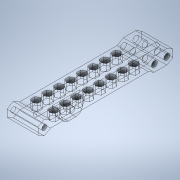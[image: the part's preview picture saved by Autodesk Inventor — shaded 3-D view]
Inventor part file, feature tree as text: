
AUTODESK INVENTOR PART (.ipt)
format: ipt  version: 2020 (Build 240168000, 168)  size: 540,672 bytes
history: native  units: in
note: dims shown in document units (in); Inventor stores cm internally (conversion verified against a paired STEP export)
features: sketch x7, extrude x6, projected_geometry x4, plane x2, mirror x1, fillet x1
ambient origin geometry x8: Origin, YZ Plane, XZ Plane, XY Plane, X Axis, Y Axis, Z Axis, Center Point
bodies: Solid1 (feature_tree)
feature tree (21):
  extrude  "Extrusion1"  Depth=3.4256in
  plane  "Work Plane1"
  extrude  "Extrusion2"  Depth=0.7874in
  sketch  "Sketch4"  dims[d4=0.0in d5=0.0984in]
  extrude  "Extrusion4"  Depth=0.0984in
  plane  "Work Plane2"
  extrude  "Extrusion6"  Depth=3.1106in
  mirror  "Mirror2"
  extrude  "Extrusion7"  Depth=0.315in
  extrude  "Extrusion8"  Depth=0.2362in
  fillet  "Fillet1"  [1 undecoded]
  sketch  "Sketch1"  dims[d0=0.1818in d1=3.4256in]
  sketch  "Sketch2"  dims[d2=0.122in d3=0.7874in]
  sketch  "Sketch5"  dims[d6=0.7874in d7=0.0in d28=3.1106in]
  sketch  "Sketch7"  dims[d29=0.315in d31=0.315in]
  projected_geometry  "Projected Loop7"
  projected_geometry  "Projected Loop8"
  sketch  "Sketch8"  dims[d33=0.1476in d34=0.2362in d35=0.0in]
  projected_geometry  "Projected Loop9"
  sketch  "Sketch10"  dims[d38=0.315in d39=0.2756in d40=-0.3092in d41=0.0787in d42=0.0787in d43=0.0787in d44=3.1496in d46=0.2913in d47=0.3937in d49=0.3937in d51=3.1496in d53=0.2913in d54=0.3937in d56=0.3937in d58=0.0in d59=0.0in d60=1.0994in d61=0.1378in d63=1.1811in d64=0.1575in d65=0.0in d66=0.126in d67=0.1575in]
  projected_geometry  "Projected Loop10"
note: 1 required parameter value undecoded (feature->parameter linkage not recoverable at this tier; creation-order binding heuristic only, values carry confidence <= 0.55)
